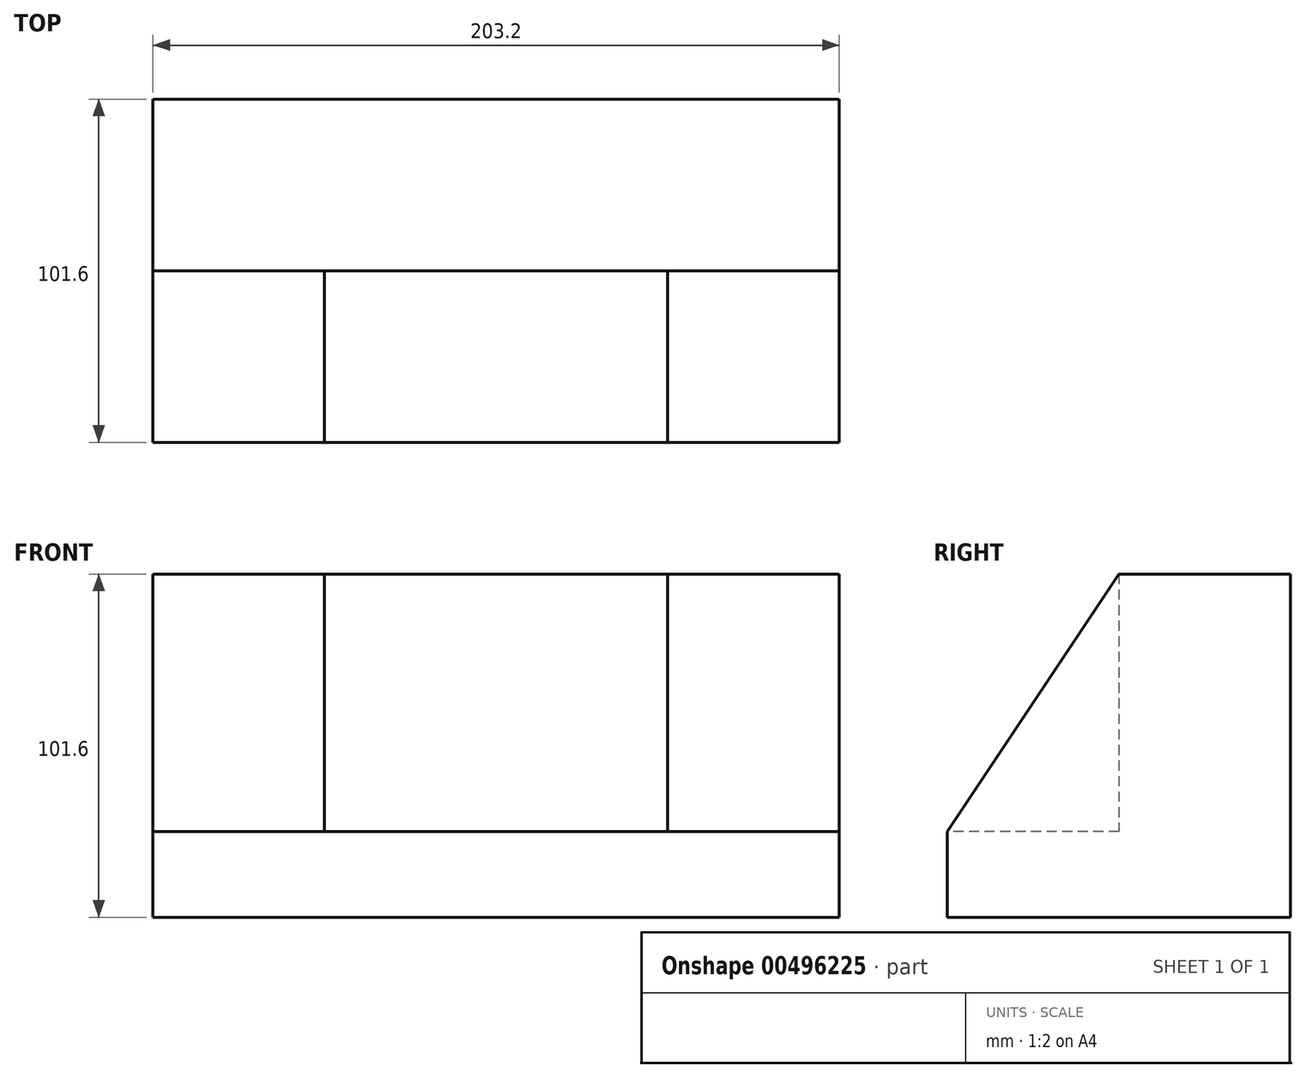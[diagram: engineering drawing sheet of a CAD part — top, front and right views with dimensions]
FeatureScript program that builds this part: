
annotation { "Feature Type Name" : "Feature", "Feature Type Description" : "" }
export const myFeature = defineFeature(function(context is Context, id is Id, definition is map)
    precondition{}
    {
        {
            var Q0;
            Q0=qCreatedBy(makeId("Top.planeOp"),FACE);
            var sketch = newSketch(context, id + "F0", { "sketchPlane" : qUnion([Q0])});
            skLineSegment(sketch, "E0.bottom", {"start": v(-126.66, 67.47) * mm, "end": v(76.54, 67.47) * mm});
            skLineSegment(sketch, "E0.top", {"start": v(-126.66, -34.13) * mm, "end": v(76.54, -34.13) * mm});
            skLineSegment(sketch, "E0.left", {"start": v(-126.66, 67.47) * mm, "end": v(-126.66, -34.13) * mm});
            skLineSegment(sketch, "E0.right", {"start": v(76.54, 67.47) * mm, "end": v(76.54, -34.13) * mm});
            skSolve(sketch);
        }
        {
            var Q0;
            Q0 = qSketchRegion(id + "F0", true);
            extrude(context, id + "F1", {"entities" : qUnion([Q0]), "depth" : 101.6 * mm});
        }
        {
            var Q0;
            Q0=makeQuery(id+"F1.opExtrude","SWEPT_FACE",FACE,{"disambiguationData":[OSD([sQuery(id+"F0.wireOp",EDGE,"E0.top")])]});
            var sketch = newSketch(context, id + "F2", { "sketchPlane" : qUnion([Q0])});
            skLineSegment(sketch, "E1.bottom", {"start": v(-75.86, 101.6) * mm, "end": v(25.74, 101.6) * mm});
            skLineSegment(sketch, "E1.top", {"start": v(-75.86, 25.4) * mm, "end": v(25.74, 25.4) * mm});
            skLineSegment(sketch, "E1.left", {"start": v(-75.86, 101.6) * mm, "end": v(-75.86, 25.4) * mm});
            skLineSegment(sketch, "E1.right", {"start": v(25.74, 101.6) * mm, "end": v(25.74, 25.4) * mm});
            skSolve(sketch);
        }
        {
            var Q0;
            Q0 = qSketchRegion(id + "F2", true);
            extrude(context, id + "F3", {"entities" : qUnion([Q0]), "operationType" : NewBodyOperationType.REMOVE, "oppositeDirection" : true, "depth" : 50.8 * mm});
        }
        {
            var Q0;
            Q0=makeQuery(id+"F1.opExtrude","SWEPT_FACE",FACE,{"disambiguationData":[OSD([sQuery(id+"F0.wireOp",EDGE,"E0.right")])]});
            var sketch = newSketch(context, id + "F4", { "sketchPlane" : qUnion([Q0])});
            skLineSegment(sketch, "E2", {"start": v(-34.13, 25.4) * mm, "end": v(16.67, 101.6) * mm});
            skLineSegment(sketch, "E3", {"start": v(16.67, 101.6) * mm, "end": v(-34.13, 101.6) * mm});
            skLineSegment(sketch, "E4", {"start": v(-34.13, 101.6) * mm, "end": v(-34.13, 25.4) * mm});
            skSolve(sketch);
        }
        {
            var Q0;
            Q0=makeQuery(id+"F4.imprint","IMPRINT",FACE,{"disambiguationData":[TD([[makeQuery(id+"F4.imprint","IMPRINT",EDGE,{"derivedFrom":sQuery(id+"F4.wireOp",EDGE,"E2")}),1.0]])]});
            extrude(context, id + "F5", {"entities" : qUnion([Q0]), "operationType" : NewBodyOperationType.REMOVE, "oppositeDirection" : true, "depth" : 203.2 * mm});
        }
    });
